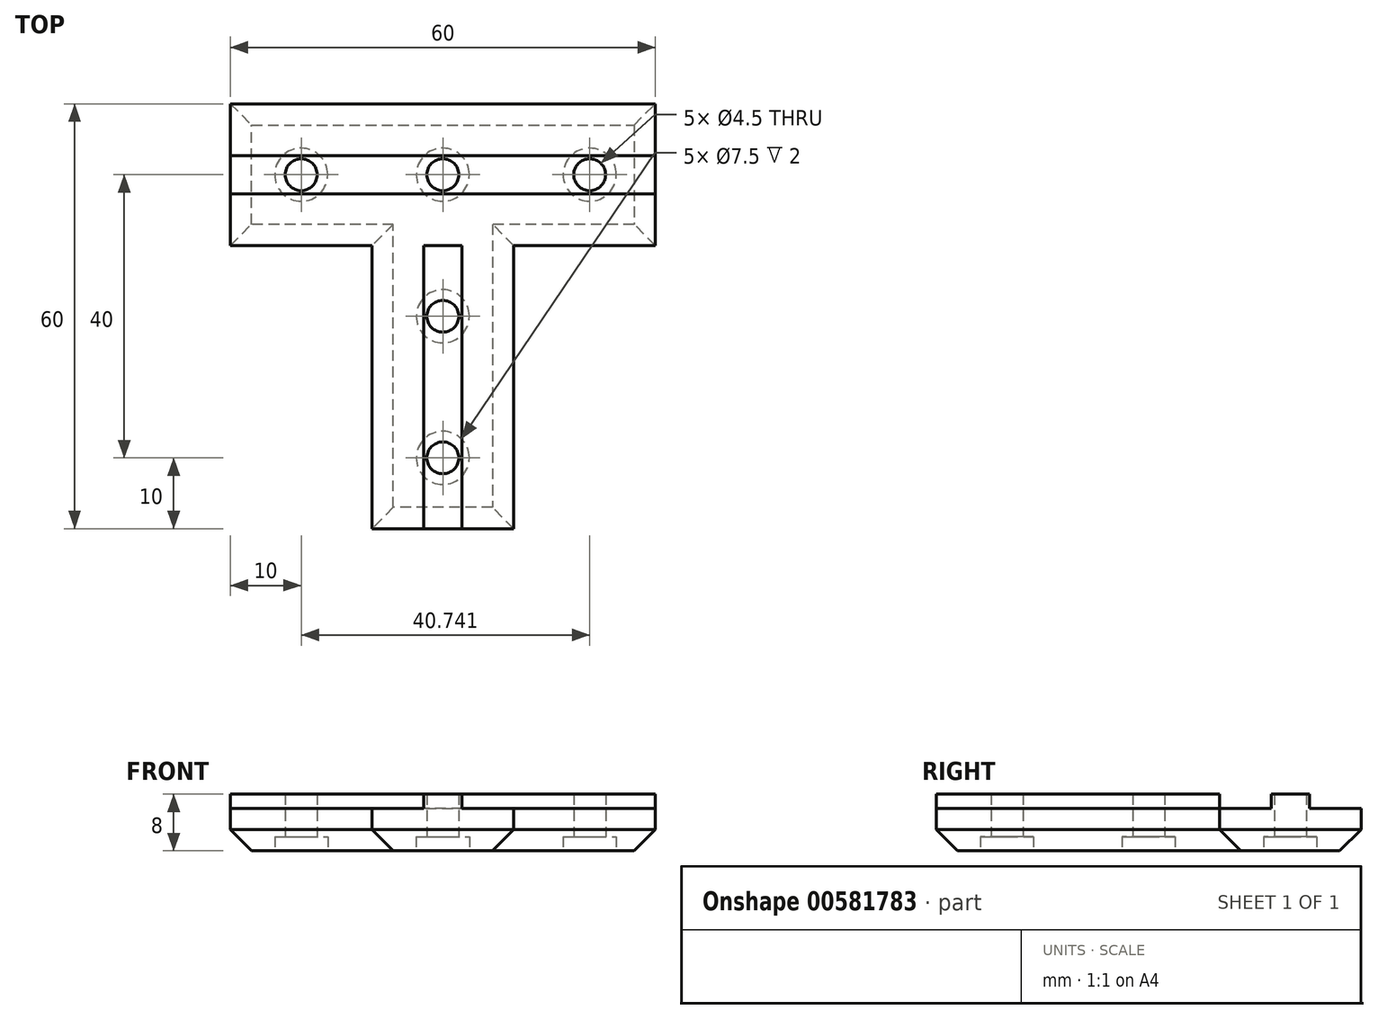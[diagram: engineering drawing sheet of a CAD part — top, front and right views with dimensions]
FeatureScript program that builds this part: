
annotation { "Feature Type Name" : "Feature", "Feature Type Description" : "" }
export const myFeature = defineFeature(function(context is Context, id is Id, definition is map)
    precondition{}
    {
        {
            var Q0;
            Q0=qCreatedBy(makeId("Top.planeOp"),FACE);
            var sketch = newSketch(context, id + "F0", { "sketchPlane" : qUnion([Q0])});
            skLineSegment(sketch, "E0", {"start": v(0, 0) * mm, "end": v(0, 20) * mm, "construction": true});
            skLineSegment(sketch, "E1", {"start": v(0, 0) * mm, "end": v(0, -40) * mm, "construction": true});
            skLineSegment(sketch, "E2", {"start": v(-10, 0) * mm, "end": v(-30, 0) * mm});
            skLineSegment(sketch, "E3", {"start": v(0, 20) * mm, "end": v(-30, 20) * mm});
            skLineSegment(sketch, "E4", {"start": v(-30, 20) * mm, "end": v(-30, 0) * mm});
            skLineSegment(sketch, "E5", {"start": v(0, 20) * mm, "end": v(30, 20) * mm});
            skLineSegment(sketch, "E6", {"start": v(30, 20) * mm, "end": v(30, 0) * mm});
            skLineSegment(sketch, "E7", {"start": v(30, 0) * mm, "end": v(10, 0) * mm});
            skLineSegment(sketch, "E8", {"start": v(0, -40) * mm, "end": v(10, -40) * mm});
            skLineSegment(sketch, "E9", {"start": v(10, -40) * mm, "end": v(10, 0) * mm});
            skLineSegment(sketch, "E10", {"start": v(0, -40) * mm, "end": v(-10, -40) * mm});
            skLineSegment(sketch, "E11", {"start": v(-10, -40) * mm, "end": v(-10, 0) * mm});
            skSolve(sketch);
        }
        {
            var Q0;
            Q0=qSketchRegion(id+"F0",true);
            extrude(context, id + "F1", {"entities" : qUnion([Q0]), "depth" : 6 * mm});
        }
        {
            var Q0;
            Q0=makeQuery(id+"F1.opExtrude","CAP_FACE",FACE,{"disambiguationData":[OSD([sQuery(id+"F0.wireOp",EDGE,"E2"),sQuery(id+"F0.wireOp",EDGE,"E3"),sQuery(id+"F0.wireOp",EDGE,"E4"),sQuery(id+"F0.wireOp",EDGE,"E5"),sQuery(id+"F0.wireOp",EDGE,"E6"),sQuery(id+"F0.wireOp",EDGE,"E7"),sQuery(id+"F0.wireOp",EDGE,"E8"),sQuery(id+"F0.wireOp",EDGE,"E9"),sQuery(id+"F0.wireOp",EDGE,"E10"),sQuery(id+"F0.wireOp",EDGE,"E11")])],"isStart":false});
            var sketch = newSketch(context, id + "F2", { "sketchPlane" : qUnion([Q0])});
            skLineSegment(sketch, "E12", {"start": v(-30, 10) * mm, "end": v(30, 10) * mm, "construction": true});
            skLineSegment(sketch, "E13", {"start": v(0, -40) * mm, "end": v(0, 0) * mm, "construction": true});
            skLineSegment(sketch, "E14", {"start": v(0, 0) * mm, "end": v(-2.71, 0) * mm});
            skLineSegment(sketch, "E15", {"start": v(-2.71, 0) * mm, "end": v(-2.7, -40) * mm});
            skLineSegment(sketch, "E16", {"start": v(2.71, -40) * mm, "end": v(2.71, 0) * mm});
            skLineSegment(sketch, "E17", {"start": v(2.71, 0) * mm, "end": v(0, 0) * mm});
            skLineSegment(sketch, "E18", {"start": v(-2.7, -40) * mm, "end": v(2.71, -40) * mm});
            skLineSegment(sketch, "E19", {"start": v(30, 12.71) * mm, "end": v(30, 7.3) * mm});
            skLineSegment(sketch, "E20", {"start": v(-30, 10) * mm, "end": v(-30, 12.71) * mm});
            skLineSegment(sketch, "E21", {"start": v(-30, 12.71) * mm, "end": v(30, 12.71) * mm});
            skLineSegment(sketch, "E22", {"start": v(-30, 10) * mm, "end": v(-30, 7.3) * mm});
            skLineSegment(sketch, "E23", {"start": v(-30, 7.3) * mm, "end": v(30, 7.3) * mm});
            skSolve(sketch);
        }
        {
            var Q0;
            Q0=qSketchRegion(id+"F2",true);
            extrude(context, id + "F3", {"entities" : qUnion([Q0]), "operationType" : NewBodyOperationType.ADD, "depth" : 2 * mm});
        }
        {
            var Q0;
            Q0=makeQuery(id+"F1.opExtrude","CAP_FACE",FACE,{"disambiguationData":[OSD([sQuery(id+"F0.wireOp",EDGE,"E2"),sQuery(id+"F0.wireOp",EDGE,"E3"),sQuery(id+"F0.wireOp",EDGE,"E4"),sQuery(id+"F0.wireOp",EDGE,"E5"),sQuery(id+"F0.wireOp",EDGE,"E6"),sQuery(id+"F0.wireOp",EDGE,"E7"),sQuery(id+"F0.wireOp",EDGE,"E8"),sQuery(id+"F0.wireOp",EDGE,"E9"),sQuery(id+"F0.wireOp",EDGE,"E10"),sQuery(id+"F0.wireOp",EDGE,"E11")])],"isStart":true});
            var sketch = newSketch(context, id + "F4", { "sketchPlane" : qUnion([Q0])});
            skCircle(sketch, "E24", {"center": v(-20, -10) * mm, "radius": 2.25 * mm});
            skCircle(sketch, "E25", {"center": v(0, 10) * mm, "radius": 2.25 * mm});
            skCircle(sketch, "E26", {"center": v(0, 30) * mm, "radius": 2.25 * mm});
            skCircle(sketch, "E27", {"center": v(20.74, -10) * mm, "radius": 2.25 * mm});
            skCircle(sketch, "E28", {"center": v(0, -10) * mm, "radius": 2.25 * mm});
            skSolve(sketch);
        }
        {
            var Q0;
            Q0=qSketchRegion(id+"F4",true);
            extrude(context, id + "F5", {"entities" : qUnion([Q0]), "operationType" : NewBodyOperationType.REMOVE, "endBound" : BoundingType.THROUGH_ALL, "oppositeDirection" : true, "depth" : 25 * mm});
        }
        {
            var Q0;
            Q0=makeQuery(id+"F1.opExtrude","CAP_FACE",FACE,{"disambiguationData":[OSD([sQuery(id+"F0.wireOp",EDGE,"E2"),sQuery(id+"F0.wireOp",EDGE,"E3"),sQuery(id+"F0.wireOp",EDGE,"E4"),sQuery(id+"F0.wireOp",EDGE,"E5"),sQuery(id+"F0.wireOp",EDGE,"E6"),sQuery(id+"F0.wireOp",EDGE,"E7"),sQuery(id+"F0.wireOp",EDGE,"E8"),sQuery(id+"F0.wireOp",EDGE,"E9"),sQuery(id+"F0.wireOp",EDGE,"E10"),sQuery(id+"F0.wireOp",EDGE,"E11")])],"isStart":true});
            var sketch = newSketch(context, id + "F6", { "sketchPlane" : qUnion([Q0])});
            skCircle(sketch, "E29", {"center": v(0, 30) * mm, "radius": 3.75 * mm});
            skCircle(sketch, "E30", {"center": v(0, 10) * mm, "radius": 3.75 * mm});
            skCircle(sketch, "E31", {"center": v(20.74, -10) * mm, "radius": 3.75 * mm});
            skCircle(sketch, "E32", {"center": v(-20, -10) * mm, "radius": 3.75 * mm});
            skCircle(sketch, "E33", {"center": v(0, -10) * mm, "radius": 3.75 * mm});
            skSolve(sketch);
        }
        {
            var Q0;
            Q0=qSketchRegion(id+"F6",true);
            extrude(context, id + "F7", {"entities" : qUnion([Q0]), "operationType" : NewBodyOperationType.REMOVE, "oppositeDirection" : true, "depth" : 2 * mm});
        }
        {
            var Q0;
            Q0=makeQuery(id+"F1.opExtrude","CAP_EDGE",EDGE,{"disambiguationData":[OSD([sQuery(id+"F0.wireOp",EDGE,"E11")])],"isStart":true});
            var Q1;
            Q1=makeQuery(id+"F1.opExtrude","CAP_EDGE",EDGE,{"disambiguationData":[OSD([sQuery(id+"F0.wireOp",EDGE,"E2")])],"isStart":true});
            var Q2;
            Q2=makeQuery(id+"F1.opExtrude","CAP_EDGE",EDGE,{"disambiguationData":[OSD([sQuery(id+"F0.wireOp",EDGE,"E9")])],"isStart":true});
            var Q3;
            Q3=makeQuery(id+"F1.opExtrude","CAP_EDGE",EDGE,{"disambiguationData":[OSD([sQuery(id+"F0.wireOp",EDGE,"E7")])],"isStart":true});
            var Q4;
            Q4=makeQuery(id+"F1.opExtrude","CAP_EDGE",EDGE,{"disambiguationData":[OSD([sQuery(id+"F0.wireOp",EDGE,"E3"),sQuery(id+"F0.wireOp",EDGE,"E5")])],"isStart":true});
            var Q5;
            Q5=makeQuery(id+"F1.opExtrude","CAP_EDGE",EDGE,{"disambiguationData":[OSD([sQuery(id+"F0.wireOp",EDGE,"E6")])],"isStart":true});
            var Q6;
            Q6=makeQuery(id+"F1.opExtrude","CAP_EDGE",EDGE,{"disambiguationData":[OSD([sQuery(id+"F0.wireOp",EDGE,"E4")])],"isStart":true});
            var Q7;
            Q7=makeQuery(id+"F1.opExtrude","CAP_EDGE",EDGE,{"disambiguationData":[OSD([sQuery(id+"F0.wireOp",EDGE,"E8"),sQuery(id+"F0.wireOp",EDGE,"E10")])],"isStart":true});
            chamfer(context, id + "F8", {"entities" : qUnion([Q0, Q1, Q2, Q3, Q4, Q5, Q6, Q7]), "width" : 3 * mm, "tangentPropagation" : true});
        }
    });
